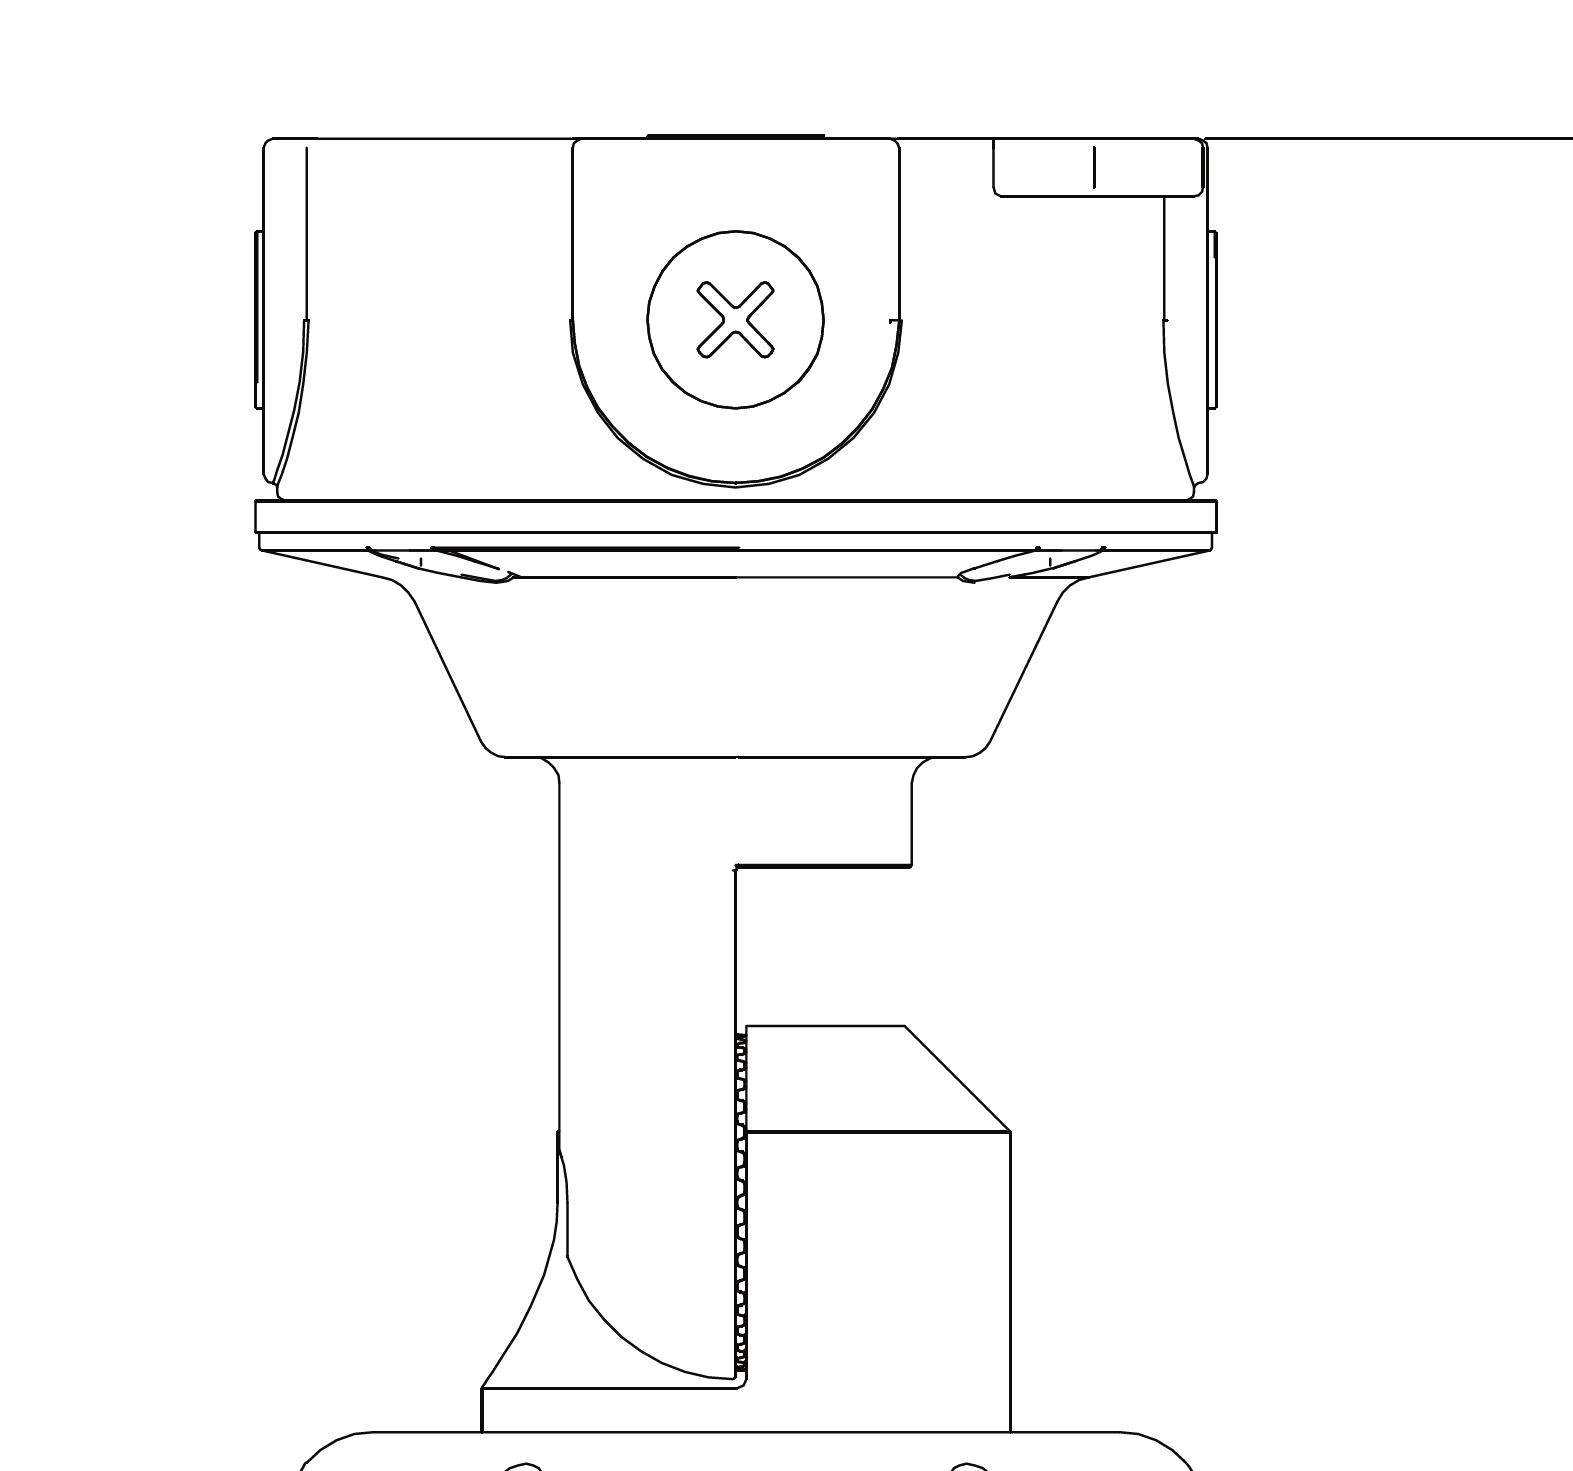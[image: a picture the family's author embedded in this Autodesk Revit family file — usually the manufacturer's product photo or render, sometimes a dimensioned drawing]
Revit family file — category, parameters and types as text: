
# Revit family: Jelly Jar_Wall&Ceiling_20W_3000K&4000K&5000K
name_source: partatom
category: Lighting Fixtures
units: mm (PartAtom-declared; Revit-internal decimal feet)

## family parameters
Always vertical = No
Cut with Voids When Loaded = No
Light Source = No
Maintain Annotation Orientation = No
Part Type = Normal
Room Calculation Point = No
Round Connector Dimension = Use Diameter
Shared = No
Work Plane-Based = No

## types (6) — shared parameters
CRI = 80
Default Elevation = 0' - 0"
Description = Jelly Jar LED Vapor Proof Light
IP Rating = 65
Input Voltage = 120-277V
Lamp = LED
Load Classification = Lighting
Manufacturer = Above All Lighting
Model = JJR20LEDSW1-CWM-GY
Power Factor = 0.9
URL = https://www.abovealllighting.com
Wattage = 20W

## per-type parameters (varying)
| type | CCT | Ceiling Mount | Lumen Output | Luminaire | Wall Mount |
| Jelly Jar_Wall Mount_20W_3000K | 3000K | No | 1700lx | Luminaire : 3000K | Yes |
| Jelly Jar_Ceiling Mount_20W_3000K | 3000K | Yes | 1700lx | Luminaire : 3000K | No |
| Jelly Jar_Wall Mount_20W_4000K | 4000K | No | 1900lx | Luminaire : 4000K | Yes |
| Jelly Jar_Wall Mount_20W_5000K | 5000K | No | 1800lx | Luminaire : 5000K | Yes |
| Jelly Jar_Ceiling Mount_20W_4000K | 4000K | Yes | 1900lx | Luminaire : 4000K | No |
| Jelly Jar_Ceiling Mount_20W_5000K | 5000K | Yes | 1800lx | Luminaire : 5000K | No |

## geometry (parser evidence)
native form markers: Sweep x5
no freeform markers — native parametric forms only
